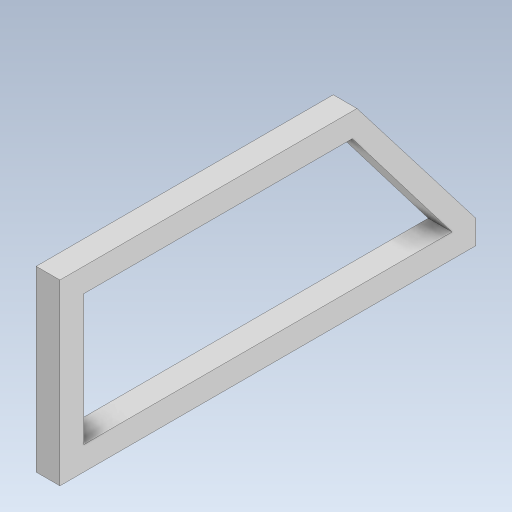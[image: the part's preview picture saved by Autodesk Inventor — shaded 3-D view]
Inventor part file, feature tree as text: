
AUTODESK INVENTOR PART (.ipt)
format: ipt  version: 2023.5 (Build 275446000, 446)  size: 101,376 bytes
history: native  units: in
note: dims shown in document units (in); Inventor stores cm internally (conversion verified against a paired STEP export)
features: extrude x1, sketch x1
ambient origin geometry x8: Origin, YZ Plane, XZ Plane, XY Plane, X Axis, Y Axis, Z Axis, Center Point
bodies: Solid1 (feature_tree)
feature tree (2):
  extrude  "Extrusion1"  Depth=2.7559in
  sketch  "Sketch1"  dims[d0=0.1575in d1=2.7559in d2=1.1811in d3=0.1575in d4=0.1575in d5=1.9685in d6=0.1575in d7=0.1575in d8=0.0in]
